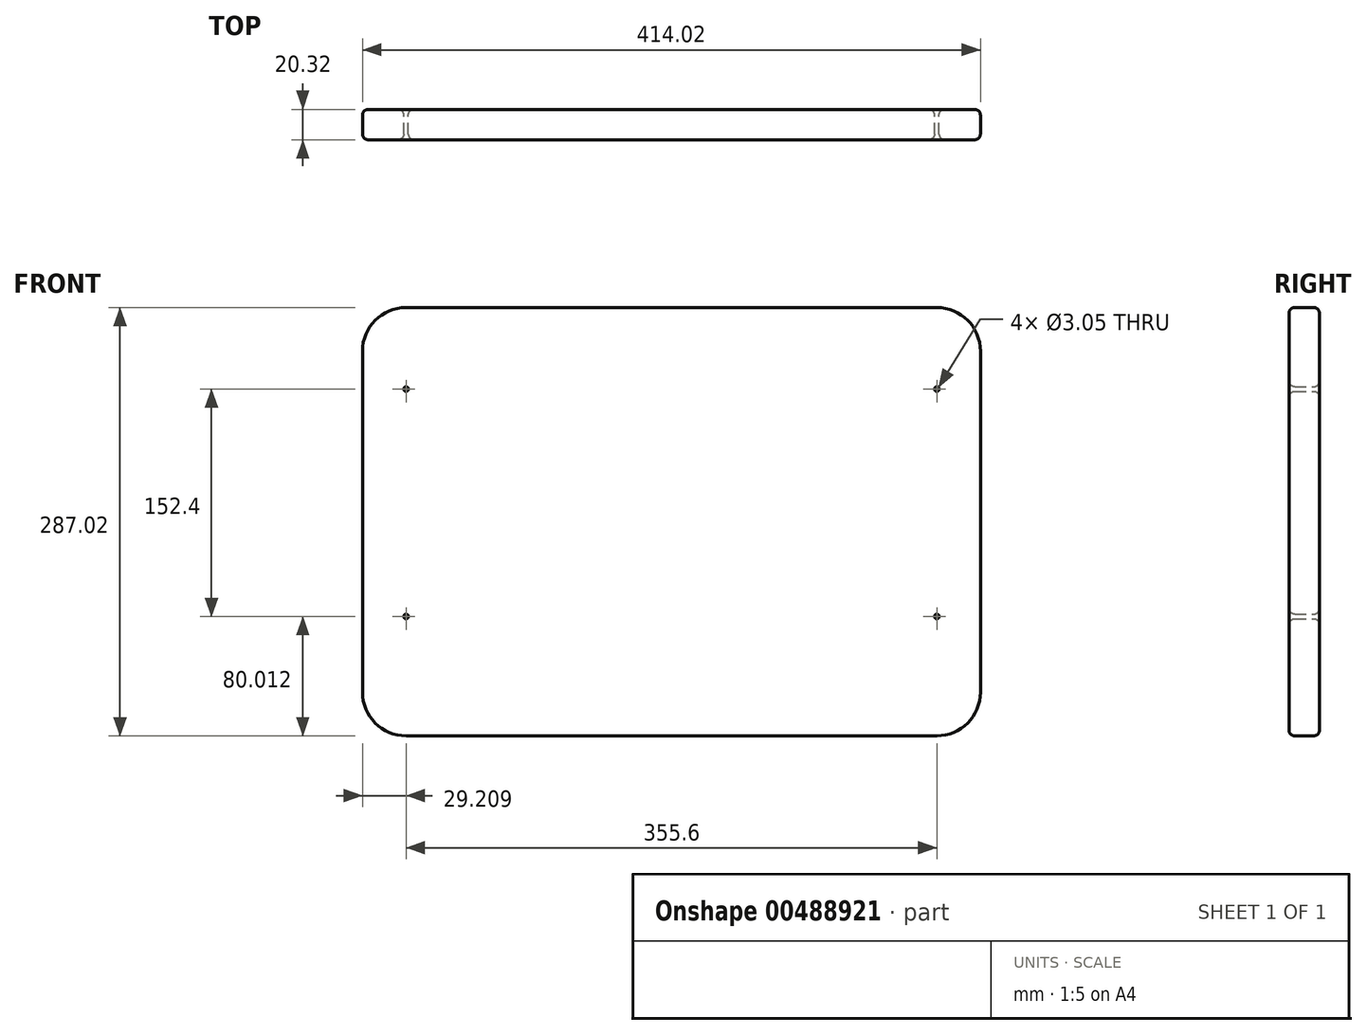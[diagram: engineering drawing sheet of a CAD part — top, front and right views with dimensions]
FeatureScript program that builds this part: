
annotation { "Feature Type Name" : "Feature", "Feature Type Description" : "" }
export const myFeature = defineFeature(function(context is Context, id is Id, definition is map)
    precondition{}
    {
        {
            var Q0;
            Q0=qCreatedBy(makeId("Front.planeOp"),FACE);
            var sketch = newSketch(context, id + "F0", { "sketchPlane" : qUnion([Q0])});
            skLineSegment(sketch, "E0.top", {"start": v(-225.84, -123.05) * mm, "end": v(129.76, -123.05) * mm});
            skArc(sketch, "E1", {"start": v(-255.05, 105.55) * mm, "mid": v(-246.5, 126.2) * mm, "end": v(-225.84, 134.76) * mm});
            skArc(sketch, "E2", {"start": v(129.76, 134.76) * mm, "mid": v(150.41, 126.2) * mm, "end": v(158.97, 105.55) * mm});
            skArc(sketch, "E3", {"start": v(158.97, -123.05) * mm, "mid": v(150.41, -143.7) * mm, "end": v(129.76, -152.26) * mm});
            skArc(sketch, "E4", {"start": v(-225.84, -152.26) * mm, "mid": v(-246.5, -143.7) * mm, "end": v(-255.05, -123.05) * mm});
            skLineSegment(sketch, "E5", {"start": v(-255.05, 105.55) * mm, "end": v(-255.05, -123.05) * mm});
            skLineSegment(sketch, "E6", {"start": v(-225.84, 134.76) * mm, "end": v(129.76, 134.76) * mm});
            skLineSegment(sketch, "E7", {"start": v(158.97, 105.55) * mm, "end": v(158.97, -123.05) * mm});
            skLineSegment(sketch, "E8", {"start": v(129.76, -152.26) * mm, "end": v(-225.84, -152.26) * mm});
            skLineSegment(sketch, "E9", {"start": v(129.76, -72.25) * mm, "end": v(129.76, -123.05) * mm});
            skLineSegment(sketch, "E10", {"start": v(129.76, -72.25) * mm, "end": v(-225.84, -72.25) * mm});
            skCircle(sketch, "E11", {"center": v(-225.84, -72.25) * mm, "radius": 1.52 * mm});
            skCircle(sketch, "E12", {"center": v(129.76, -72.25) * mm, "radius": 1.52 * mm});
            skLineSegment(sketch, "E13", {"start": v(129.76, -72.25) * mm, "end": v(129.76, 80.15) * mm});
            skLineSegment(sketch, "E14", {"start": v(129.76, 80.15) * mm, "end": v(-225.84, 80.15) * mm});
            skCircle(sketch, "E15", {"center": v(-225.84, 80.15) * mm, "radius": 1.52 * mm});
            skCircle(sketch, "E16", {"center": v(129.76, 80.15) * mm, "radius": 1.52 * mm});
            skSolve(sketch);
        }
        {
            var Q0;
            Q0 = qSketchRegion(id + "F0", true);
            extrude(context, id + "F1", {"entities" : qUnion([Q0]), "endBound" : BoundingType.SYMMETRIC, "depth" : 20.32 * mm});
        }
        {
            var Q0;
            Q0=makeQuery(id+"F1.opExtrude","CAP_FACE",FACE,{"disambiguationData":[OSD([sQuery(id+"F0.wireOp",EDGE,"E1"),sQuery(id+"F0.wireOp",EDGE,"E2"),sQuery(id+"F0.wireOp",EDGE,"E3"),sQuery(id+"F0.wireOp",EDGE,"E4"),sQuery(id+"F0.wireOp",EDGE,"E5"),sQuery(id+"F0.wireOp",EDGE,"E6"),sQuery(id+"F0.wireOp",EDGE,"E7"),sQuery(id+"F0.wireOp",EDGE,"E8"),sQuery(id+"F0.wireOp",EDGE,"0FQYNTrz-RV7O-u1NF-qqTG-l8T6v7UB5ISa"),sQuery(id+"F0.wireOp",EDGE,"E11"),sQuery(id+"F0.wireOp",EDGE,"E12"),sQuery(id+"F0.wireOp",EDGE,"7kBDwmSe-fRY9-U4Do-3EVp-J7jwr0qC9PCR")])],"isStart":false});
            var Q1;
            Q1=makeQuery(id+"F1.opExtrude","CAP_FACE",FACE,{"disambiguationData":[OSD([sQuery(id+"F0.wireOp",EDGE,"E1"),sQuery(id+"F0.wireOp",EDGE,"E2"),sQuery(id+"F0.wireOp",EDGE,"E3"),sQuery(id+"F0.wireOp",EDGE,"E4"),sQuery(id+"F0.wireOp",EDGE,"E5"),sQuery(id+"F0.wireOp",EDGE,"E6"),sQuery(id+"F0.wireOp",EDGE,"E7"),sQuery(id+"F0.wireOp",EDGE,"E8"),sQuery(id+"F0.wireOp",EDGE,"0FQYNTrz-RV7O-u1NF-qqTG-l8T6v7UB5ISa"),sQuery(id+"F0.wireOp",EDGE,"E11"),sQuery(id+"F0.wireOp",EDGE,"E12"),sQuery(id+"F0.wireOp",EDGE,"7kBDwmSe-fRY9-U4Do-3EVp-J7jwr0qC9PCR")])],"isStart":true});
            fillet(context, id + "F2", {"entities" : qUnion([Q0, Q1]), "radius" : 3.8 * mm, "tangentPropagation" : true, "allowEdgeOverflow" : false});
        }
    });
